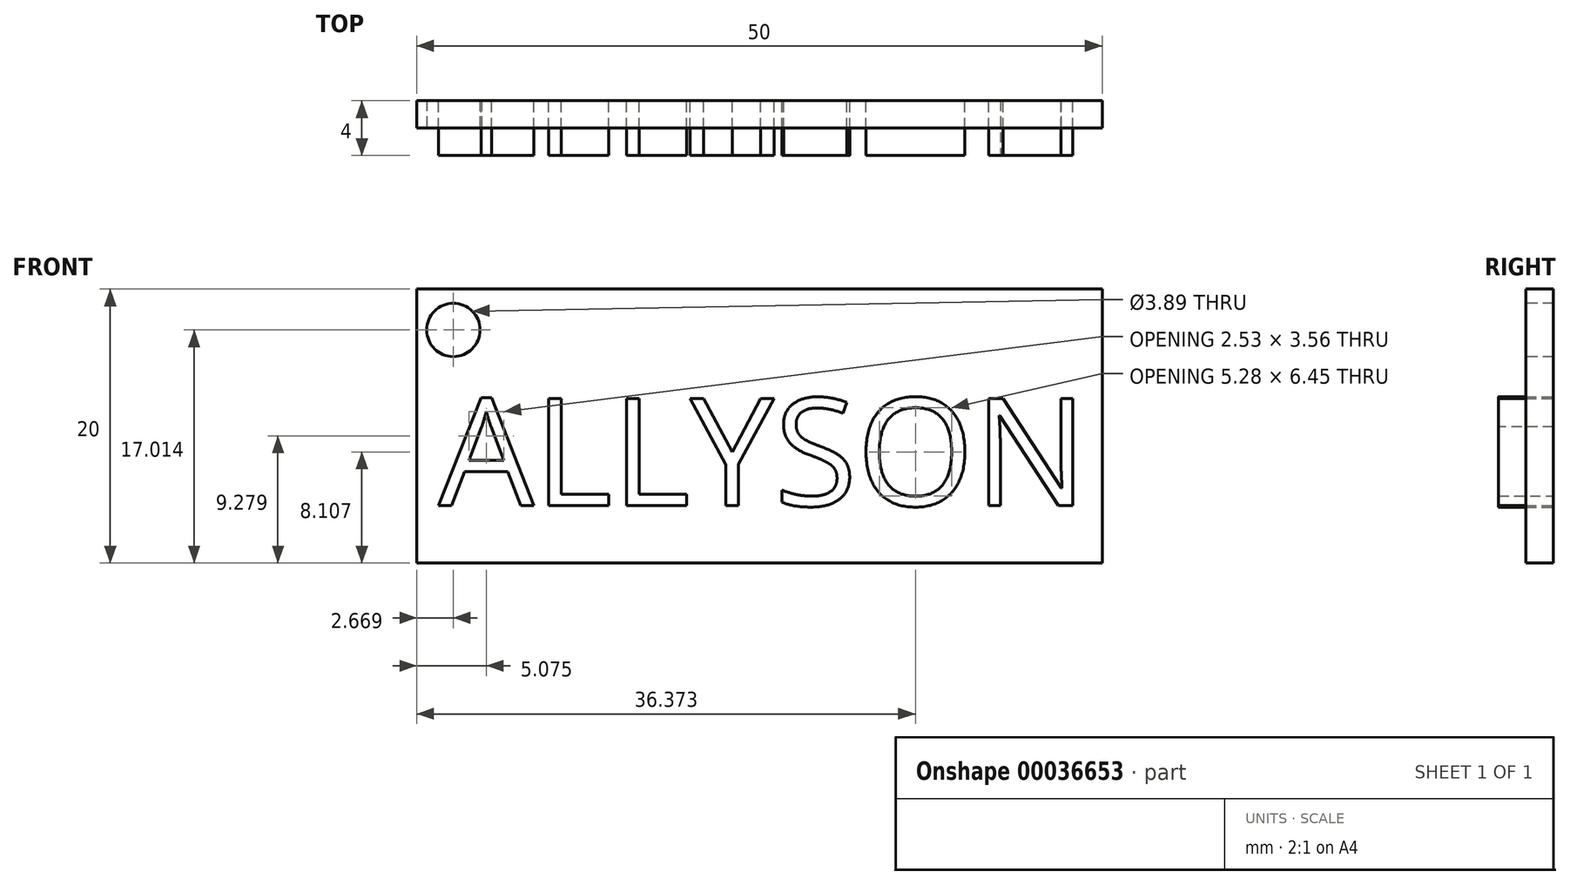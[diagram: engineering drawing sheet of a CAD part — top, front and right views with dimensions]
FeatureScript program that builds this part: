
annotation { "Feature Type Name" : "Feature", "Feature Type Description" : "" }
export const myFeature = defineFeature(function(context is Context, id is Id, definition is map)
    precondition{}
    {
        {
            var Q0;
            Q0=qCreatedBy(makeId("Front.planeOp"),FACE);
            var sketch = newSketch(context, id + "F0", { "sketchPlane" : qUnion([Q0])});
            skLineSegment(sketch, "E0.bottom", {"start": v(-50.3, 47.43) * mm, "end": v(77.18, 47.43) * mm});
            skLineSegment(sketch, "E0.top", {"start": v(-50.3, 0) * mm, "end": v(77.18, 0) * mm});
            skLineSegment(sketch, "E0.left", {"start": v(-50.3, 47.43) * mm, "end": v(-50.3, 0) * mm});
            skLineSegment(sketch, "E0.right", {"start": v(77.18, 47.43) * mm, "end": v(77.18, 0) * mm});
            skCircle(sketch, "E1", {"center": v(-46.98, 25.39) * mm, "radius": 3.06 * mm});
            skText(sketch, "E2", { "text": "ALLYSON", "fontName": "OpenSans-Regular.ttf"});
            const initialGuessF0  = {"E2": [-0.04342, 0.0107, 1, 0, 0.0206]};
            skSetInitialGuess(sketch, initialGuessF0);
            skSolve(sketch);
        }
        {
            var Q0;
            Q0=qCreatedBy(makeId("Front.planeOp"),FACE);
            var sketch = newSketch(context, id + "F1", { "sketchPlane" : qUnion([Q0])});
            skLineSegment(sketch, "E3.bottom", {"start": v(-9.8, 35.78) * mm, "end": v(40.2, 35.78) * mm});
            skLineSegment(sketch, "E3.top", {"start": v(-9.8, 15.78) * mm, "end": v(40.2, 15.78) * mm});
            skLineSegment(sketch, "E3.left", {"start": v(-9.8, 35.78) * mm, "end": v(-9.8, 15.78) * mm});
            skLineSegment(sketch, "E3.right", {"start": v(40.2, 35.78) * mm, "end": v(40.2, 15.78) * mm});
            skText(sketch, "E4", { "text": "ALLYSON", "fontName": "OpenSans-Regular.ttf"});
            const initialGuessF1  = {"E4": [-0.00803, 0.01975, 1, 0, 0.0079]};
            skSetInitialGuess(sketch, initialGuessF1);
            skSolve(sketch);
        }
        {
            var Q0;
            Q0=makeQuery(id+"F1.imprint","IMPRINT",FACE,{"disambiguationData":[TD([[makeQuery(id+"F1.imprint","IMPRINT",EDGE,{"derivedFrom":sQuery(id+"F1.wireOp",EDGE,"E4.sketch_text.stroke-0")}),-1.0]])]});
            var Q1;
            Q1=makeQuery(id+"F1.imprint","IMPRINT",FACE,{"disambiguationData":[TD([[makeQuery(id+"F1.imprint","IMPRINT",EDGE,{"derivedFrom":sQuery(id+"F1.wireOp",EDGE,"E4.sketch_text.stroke-13")}),-1.0]])]});
            var Q2;
            Q2=makeQuery(id+"F1.imprint","IMPRINT",FACE,{"disambiguationData":[TD([[makeQuery(id+"F1.imprint","IMPRINT",EDGE,{"derivedFrom":sQuery(id+"F1.wireOp",EDGE,"E4.sketch_text.stroke-19")}),-1.0]])]});
            var Q3;
            Q3=makeQuery(id+"F1.imprint","IMPRINT",FACE,{"disambiguationData":[TD([[makeQuery(id+"F1.imprint","IMPRINT",EDGE,{"derivedFrom":sQuery(id+"F1.wireOp",EDGE,"E4.sketch_text.stroke-25")}),-1.0]])]});
            var Q4;
            Q4=makeQuery(id+"F1.imprint","IMPRINT",FACE,{"disambiguationData":[TD([[makeQuery(id+"F1.imprint","IMPRINT",EDGE,{"derivedFrom":sQuery(id+"F1.wireOp",EDGE,"E4.sketch_text.stroke-34")}),-1.0]])]});
            var Q5;
            Q5=makeQuery(id+"F1.imprint","IMPRINT",FACE,{"disambiguationData":[TD([[makeQuery(id+"F1.imprint","IMPRINT",EDGE,{"derivedFrom":sQuery(id+"F1.wireOp",EDGE,"E4.sketch_text.stroke-59")}),-1.0]])]});
            var Q6;
            Q6=makeQuery(id+"F1.imprint","IMPRINT",FACE,{"disambiguationData":[TD([[makeQuery(id+"F1.imprint","IMPRINT",EDGE,{"derivedFrom":sQuery(id+"F1.wireOp",EDGE,"E4.sketch_text.stroke-75")}),-1.0]])]});
            extrude(context, id + "F2", {"entities" : qUnion([Q0, Q1, Q2, Q3, Q4, Q5, Q6]), "depth" : 4 * mm});
        }
        {
            var Q0;
            Q0=qCreatedBy(makeId("Front.planeOp"),FACE);
            var sketch = newSketch(context, id + "F3", { "sketchPlane" : qUnion([Q0])});
            skLineSegment(sketch, "E5.bottom", {"start": v(-9.63, 35.56) * mm, "end": v(40.37, 35.56) * mm});
            skLineSegment(sketch, "E5.top", {"start": v(-9.63, 15.56) * mm, "end": v(40.37, 15.56) * mm});
            skLineSegment(sketch, "E5.left", {"start": v(-9.63, 35.56) * mm, "end": v(-9.63, 15.56) * mm});
            skLineSegment(sketch, "E5.right", {"start": v(40.37, 35.56) * mm, "end": v(40.37, 15.56) * mm});
            skSolve(sketch);
        }
        {
            var Q0;
            Q0=makeQuery(id+"F3.imprint","IMPRINT",FACE,{"disambiguationData":[TD([[makeQuery(id+"F3.imprint","IMPRINT",EDGE,{"derivedFrom":sQuery(id+"F3.wireOp",EDGE,"E5.bottom")}),-1.0]])]});
            extrude(context, id + "F4", {"entities" : qUnion([Q0]), "depth" : 2 * mm});
        }
        {
            var Q0;
            Q0=makeQuery(id+"F4.opExtrude","CAP_FACE",FACE,{"disambiguationData":[OSD([sQuery(id+"F3.wireOp",EDGE,"E5.bottom"),sQuery(id+"F3.wireOp",EDGE,"E5.top"),sQuery(id+"F3.wireOp",EDGE,"E5.left"),sQuery(id+"F3.wireOp",EDGE,"E5.right")])],"isStart":false});
            var sketch = newSketch(context, id + "F5", { "sketchPlane" : qUnion([Q0])});
            skCircle(sketch, "E6", {"center": v(-6.96, 32.57) * mm, "radius": 1.95 * mm});
            skSolve(sketch);
        }
        {
            var Q0;
            Q0=makeQuery(id+"F5.imprint","IMPRINT",FACE,{"disambiguationData":[TD([[makeQuery(id+"F5.imprint","IMPRINT",EDGE,{"derivedFrom":sQuery(id+"F5.wireOp",EDGE,"E6")}),1.0]])]});
            extrude(context, id + "F6", {"entities" : qUnion([Q0]), "operationType" : NewBodyOperationType.REMOVE, "endBound" : BoundingType.THROUGH_ALL, "oppositeDirection" : true, "depth" : 25 * mm});
        }
    });
